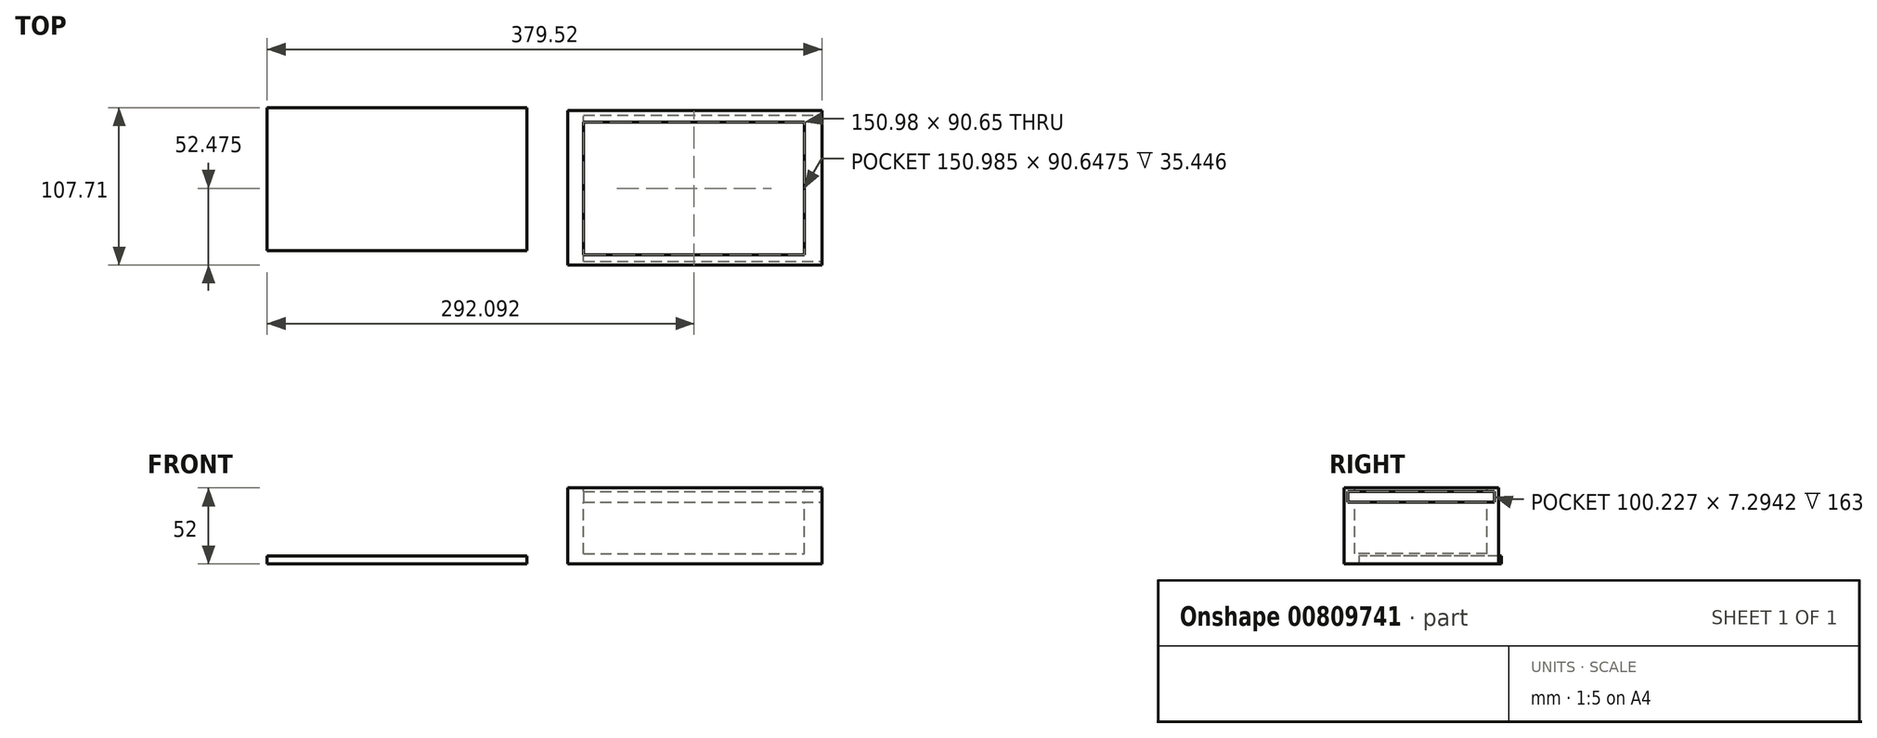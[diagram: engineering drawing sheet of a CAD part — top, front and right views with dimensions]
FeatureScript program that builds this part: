
annotation { "Feature Type Name" : "Feature", "Feature Type Description" : "" }
export const myFeature = defineFeature(function(context is Context, id is Id, definition is map)
    precondition{}
    {
        {
            var Q0;
            Q0=qCreatedBy(makeId("Top.planeOp"),FACE);
            var sketch = newSketch(context, id + "F0", { "sketchPlane" : qUnion([Q0])});
            skLineSegment(sketch, "E0.bottom", {"start": v(-46.21, 36.4) * mm, "end": v(127.62, 36.4) * mm});
            skLineSegment(sketch, "E0.top", {"start": v(-46.21, -69.33) * mm, "end": v(127.62, -69.33) * mm});
            skLineSegment(sketch, "E0.left", {"start": v(-46.21, 36.4) * mm, "end": v(-46.21, -69.33) * mm});
            skLineSegment(sketch, "E0.right", {"start": v(127.62, 36.4) * mm, "end": v(127.62, -69.33) * mm});
            skSolve(sketch);
        }
        {
            var Q0;
            Q0=makeQuery(id+"F0.imprint","IMPRINT",FACE,{"disambiguationData":[TD([[makeQuery(id+"F0.imprint","IMPRINT",EDGE,{"derivedFrom":sQuery(id+"F0.wireOp",EDGE,"E0.bottom")}),-1.0]])]});
            extrude(context, id + "F1", {"entities" : qUnion([Q0]), "depth" : 52 * mm, "offsetDistance" : 25 * mm});
        }
        {
            var Q0;
            Q0=makeQuery(id+"F1.opExtrude","CAP_FACE",FACE,{"disambiguationData":[OSD([sQuery(id+"F0.wireOp",EDGE,"E0.bottom"),sQuery(id+"F0.wireOp",EDGE,"E0.top"),sQuery(id+"F0.wireOp",EDGE,"E0.left"),sQuery(id+"F0.wireOp",EDGE,"E0.right")])],"isStart":false});
            var sketch = newSketch(context, id + "F2", { "sketchPlane" : qUnion([Q0])});
            skLineSegment(sketch, "E1.bottom", {"start": v(-35.3, 28.47) * mm, "end": v(115.68, 28.47) * mm});
            skLineSegment(sketch, "E1.top", {"start": v(-35.3, -62.18) * mm, "end": v(115.68, -62.18) * mm});
            skLineSegment(sketch, "E1.left", {"start": v(-35.3, 28.47) * mm, "end": v(-35.3, -62.18) * mm});
            skLineSegment(sketch, "E1.right", {"start": v(115.68, 28.47) * mm, "end": v(115.68, -62.18) * mm});
            skSolve(sketch);
        }
        {
            var Q0;
            Q0=makeQuery(id+"F2.imprint","IMPRINT",FACE,{"disambiguationData":[TD([[makeQuery(id+"F2.imprint","IMPRINT",EDGE,{"derivedFrom":sQuery(id+"F2.wireOp",EDGE,"E1.bottom")}),-1.0]])]});
            extrude(context, id + "F3", {"entities" : qUnion([Q0]), "operationType" : NewBodyOperationType.REMOVE, "oppositeDirection" : true, "depth" : 45.1 * mm, "offsetDistance" : 25 * mm});
        }
        {
            var Q0;
            Q0=makeQuery(id+"F1.opExtrude","SWEPT_FACE",FACE,{"disambiguationData":[OSD([sQuery(id+"F0.wireOp",EDGE,"E0.right")])]});
            var sketch = newSketch(context, id + "F4", { "sketchPlane" : qUnion([Q0])});
            skLineSegment(sketch, "E2.bottom", {"start": v(-66.9, 49.64) * mm, "end": v(33.33, 49.64) * mm});
            skLineSegment(sketch, "E2.top", {"start": v(-66.9, 42.35) * mm, "end": v(33.33, 42.35) * mm});
            skLineSegment(sketch, "E2.left", {"start": v(-66.9, 49.64) * mm, "end": v(-66.9, 42.35) * mm});
            skLineSegment(sketch, "E2.right", {"start": v(33.33, 49.64) * mm, "end": v(33.33, 42.35) * mm});
            skSolve(sketch);
        }
        {
            var Q0;
            Q0=makeQuery(id+"F4.imprint","IMPRINT",FACE,{"disambiguationData":[TD([[makeQuery(id+"F4.imprint","IMPRINT",EDGE,{"derivedFrom":sQuery(id+"F4.wireOp",EDGE,"E2.bottom")}),-1.0]])]});
            extrude(context, id + "F5", {"entities" : qUnion([Q0]), "operationType" : NewBodyOperationType.REMOVE, "oppositeDirection" : true, "depth" : 163 * mm, "offsetDistance" : 25 * mm});
        }
        {
            var Q0;
            Q0=qCreatedBy(makeId("Top.planeOp"),FACE);
            var sketch = newSketch(context, id + "F6", { "sketchPlane" : qUnion([Q0])});
            skLineSegment(sketch, "E3.bottom", {"start": v(-251.9, 38.38) * mm, "end": v(-74.02, 38.38) * mm});
            skLineSegment(sketch, "E3.top", {"start": v(-251.9, -59.34) * mm, "end": v(-74.02, -59.34) * mm});
            skLineSegment(sketch, "E3.left", {"start": v(-251.9, 38.38) * mm, "end": v(-251.9, -59.34) * mm});
            skLineSegment(sketch, "E3.right", {"start": v(-74.02, 38.38) * mm, "end": v(-74.02, -59.34) * mm});
            skSolve(sketch);
        }
        {
            var Q0;
            Q0 = qSketchRegion(id + "F6", true);
            var Q1;
            Q1=makeQuery(id+"F6.imprint","IMPRINT",FACE,{"disambiguationData":[TD([[makeQuery(id+"F6.imprint","IMPRINT",EDGE,{"derivedFrom":sQuery(id+"F6.wireOp",EDGE,"E3.bottom")}),-1.0]])]});
            extrude(context, id + "F7", {"entities" : qUnion([Q0, Q1]), "depth" : 5.5 * mm, "offsetDistance" : 25 * mm});
        }
    });
